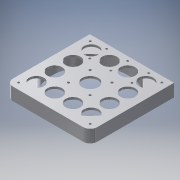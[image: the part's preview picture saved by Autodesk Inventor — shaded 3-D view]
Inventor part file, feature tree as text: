
AUTODESK INVENTOR PART (.ipt)
format: ipt  version: 2016 (Build 200138000, 138)  size: 239,104 bytes
history: native  units: mm
features: sketch x6, extrude x4, hole x2, reference x2, projected_geometry x2, thicken_offset x1
ambient origin geometry x8: Origin, YZ Plane, XZ Plane, XY Plane, X Axis, Y Axis, Z Axis, Center Point
bodies: Solid1 (feature_tree)
feature tree (17):
  extrude  "Extrusion1"  TaperAngle=0.0deg  [1 undecoded]
  extrude  "Extrusion2"  TaperAngle=0.0deg  [1 undecoded]
  extrude  "Extrusion3"  Depth=3.0mm
  hole  "Hole1"  [1 undecoded]
  thicken_offset  "Thicken1"
  hole  "Hole2"  [1 undecoded]
  extrude  "Extrusion4"  Depth=10.0mm
  sketch  "Sketch1"  dims[d0=15.0mm d1=0.0mm]
  reference  "Reference1"
  reference  "Reference2"
  sketch  "Sketch2"  dims[d2=3.0mm d3=0.0mm]
  projected_geometry  "Projected Loop1"
  sketch  "Sketch3"  dims[d4=23.0mm d5=3.0mm]
  sketch  "Sketch4"  dims[d6=0.0mm d7=31.0mm]
  sketch  "Sketch5"  dims[d8=31.0mm]
  sketch  "Sketch6"  dims[d9=3.4mm d10=6.0mm d11=4.0mm d12=2.0mm d13=90.0deg d14=8.0mm d15=20.594885mm d16=0.6mm d17=0.5mm d21=60.0mm d22=24.0mm d23=6.0mm d24=3.1mm d25=6.0mm d26=4.0mm d27=2.0mm d28=90.0deg d29=2.0mm d30=20.594885mm d32=21.0mm d37=40.0mm d39=26.0mm d40=10.0mm d42=10.0mm d44=20.0mm d46=26.0mm d47=10.0mm d49=10.0mm d51=20.0mm d53=26.0mm d54=10.0mm d56=10.0mm d59=26.0mm d60=10.0mm d61=0.0mm]
  projected_geometry  "Projected Loop2"
note: 4 required parameter values undecoded (feature->parameter linkage not recoverable at this tier; creation-order binding heuristic only, values carry confidence <= 0.55)
